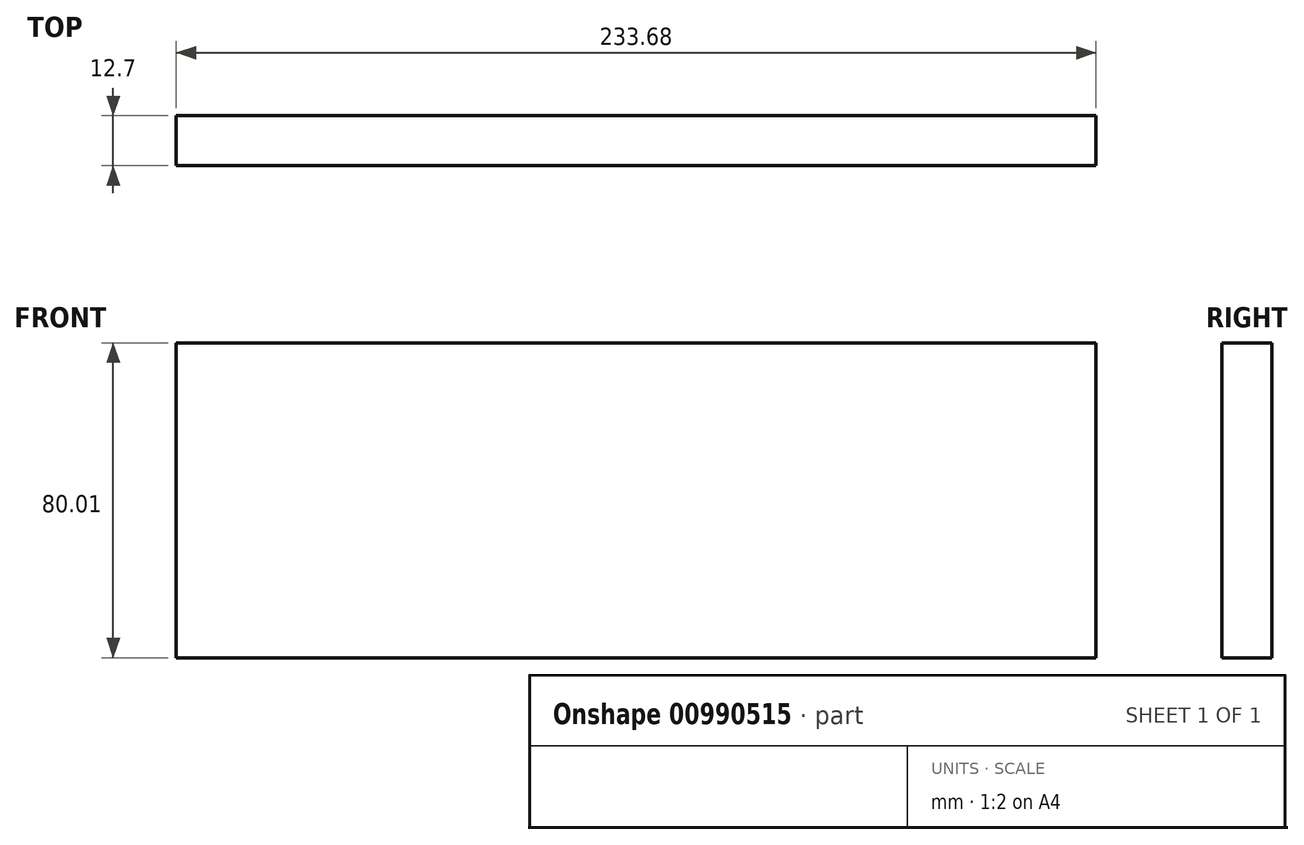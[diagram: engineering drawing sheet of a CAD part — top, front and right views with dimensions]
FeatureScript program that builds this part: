
annotation { "Feature Type Name" : "Feature", "Feature Type Description" : "" }
export const myFeature = defineFeature(function(context is Context, id is Id, definition is map)
    precondition{}
    {
        {
            var Q0;
            Q0=qCreatedBy(makeId("Front.planeOp"),FACE);
            var sketch = newSketch(context, id + "F0", { "sketchPlane" : qUnion([Q0])});
            skLineSegment(sketch, "E0.bottom", {"start": v(-168.68, -27.77) * mm, "end": v(65, -27.77) * mm});
            skLineSegment(sketch, "E0.top", {"start": v(-168.68, -107.78) * mm, "end": v(65, -107.78) * mm});
            skLineSegment(sketch, "E0.left", {"start": v(-168.68, -27.77) * mm, "end": v(-168.68, -107.78) * mm});
            skLineSegment(sketch, "E0.right", {"start": v(65, -27.77) * mm, "end": v(65, -107.78) * mm});
            skSolve(sketch);
        }
        {
            var Q0;
            Q0 = qSketchRegion(id + "F0", true);
            extrude(context, id + "F1", {"entities" : qUnion([Q0]), "depth" : 12.7 * mm, "offsetDistance" : 25.4 * mm});
        }
    });
